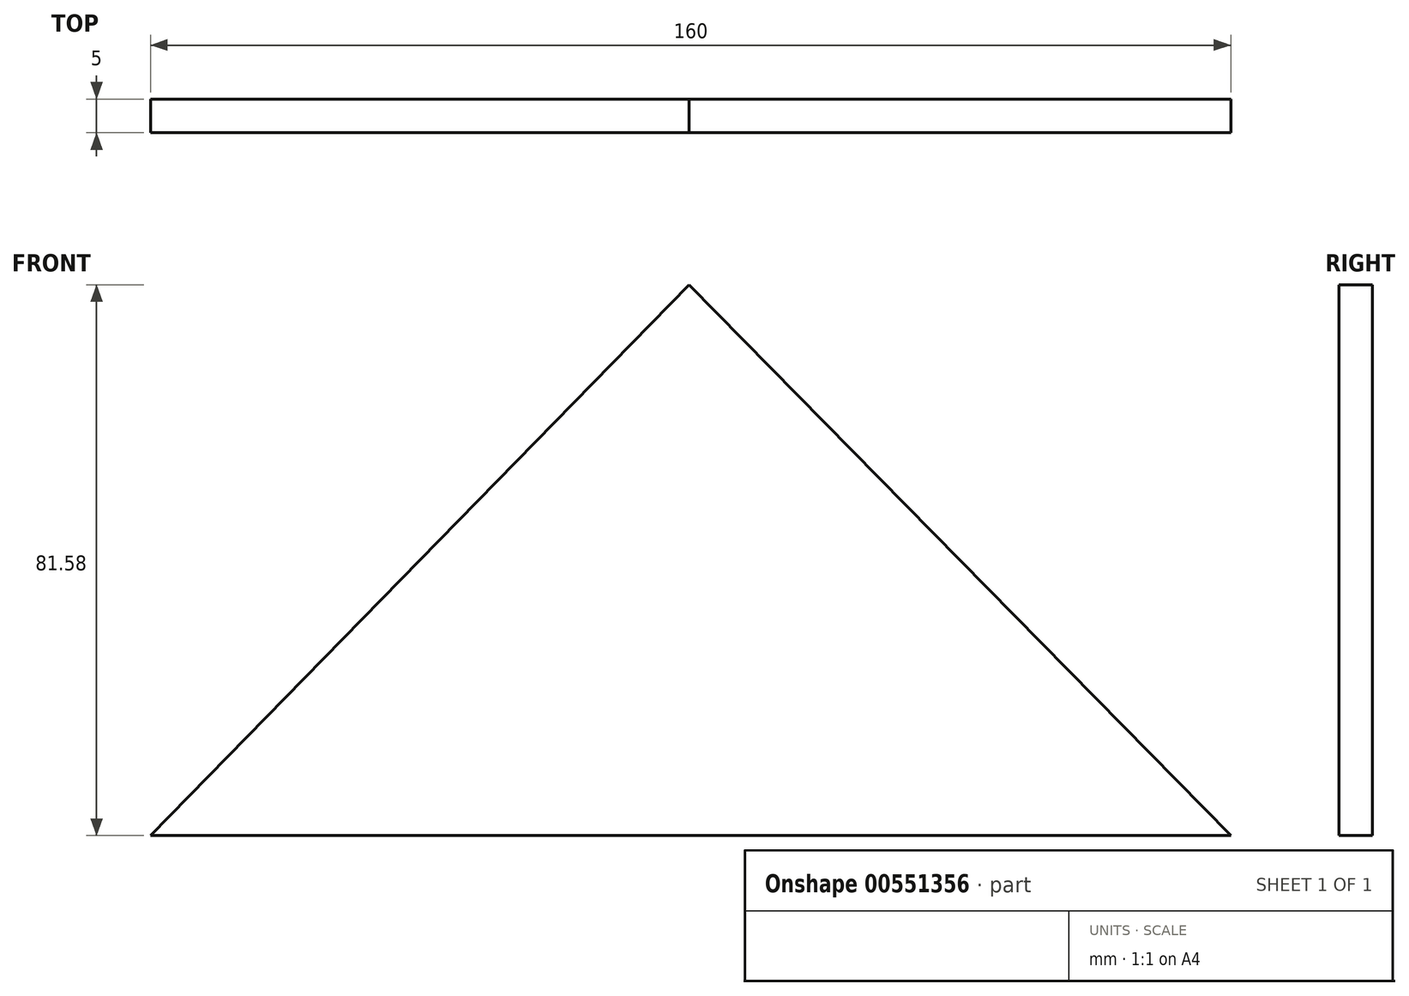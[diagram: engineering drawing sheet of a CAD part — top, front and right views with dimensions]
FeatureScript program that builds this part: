
annotation { "Feature Type Name" : "Feature", "Feature Type Description" : "" }
export const myFeature = defineFeature(function(context is Context, id is Id, definition is map)
    precondition{}
    {
        {
            var Q0;
            Q0=qCreatedBy(makeId("Front.planeOp"),FACE);
            var sketch = newSketch(context, id + "F0", { "sketchPlane" : qUnion([Q0])});
            skLineSegment(sketch, "E0", {"start": v(80.24, -36.19) * mm, "end": v(-79.76, -36.19) * mm});
            skLineSegment(sketch, "E1", {"start": v(-79.76, -36.19) * mm, "end": v(0, 45.39) * mm});
            skLineSegment(sketch, "E2", {"start": v(0, 45.39) * mm, "end": v(80.24, -36.19) * mm});
            skSolve(sketch);
        }
        {
            var Q0;
            Q0 = qSketchRegion(id + "F0", true);
            extrude(context, id + "F1", {"entities" : qUnion([Q0]), "depth" : 5 * mm, "offsetDistance" : 25 * mm});
        }
    });
